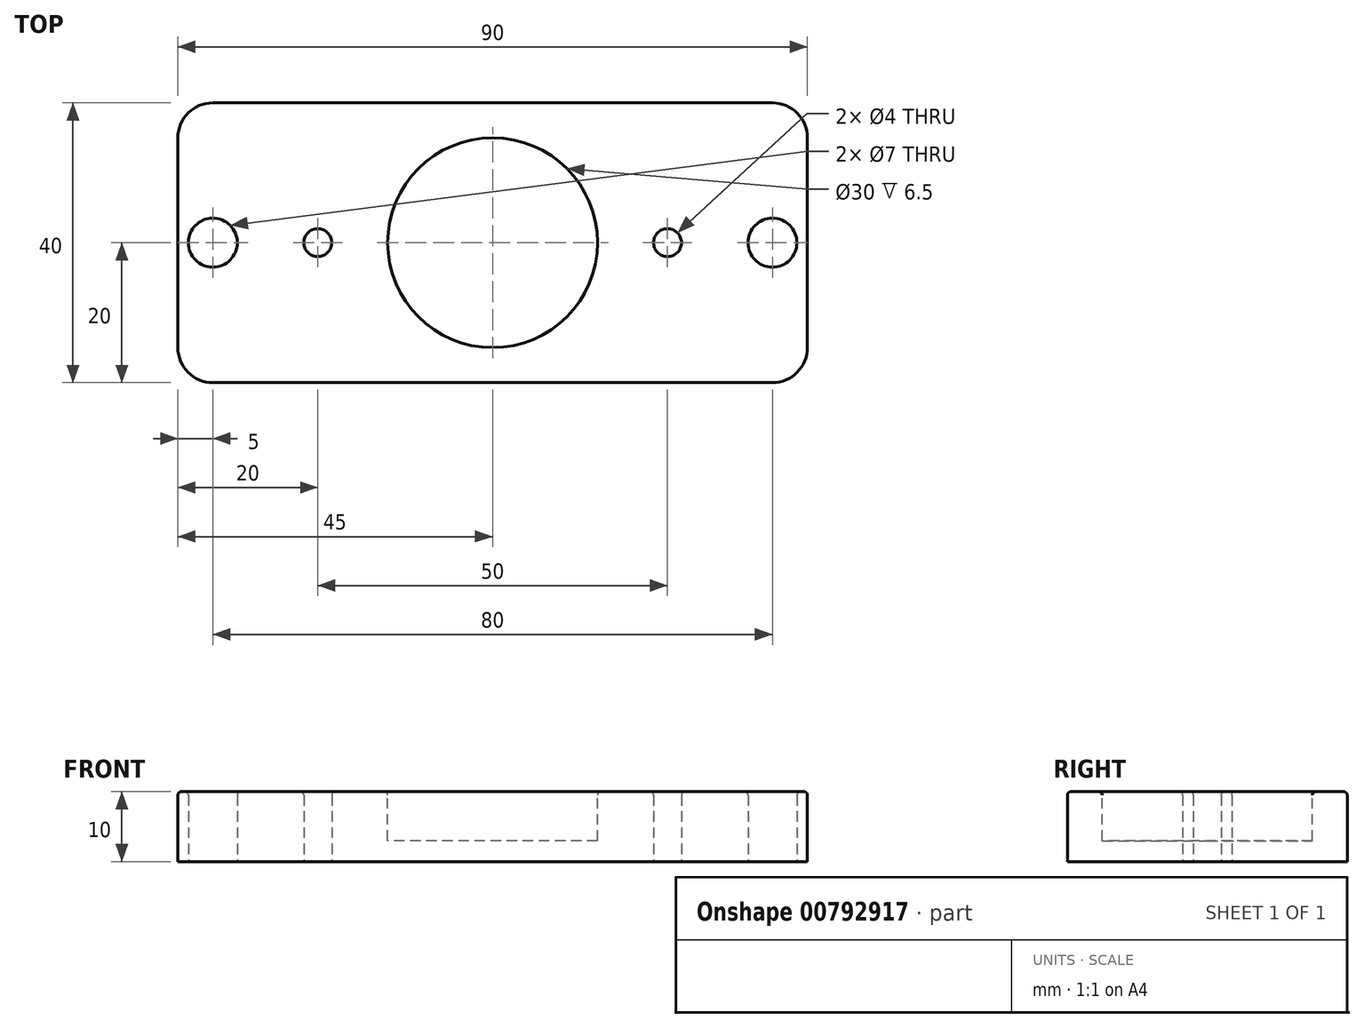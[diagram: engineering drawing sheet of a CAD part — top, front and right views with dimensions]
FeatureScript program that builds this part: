
annotation { "Feature Type Name" : "Feature", "Feature Type Description" : "" }
export const myFeature = defineFeature(function(context is Context, id is Id, definition is map)
    precondition{}
    {
        {
            var Q0;
            Q0=qCreatedBy(makeId("Top.planeOp"),FACE);
            var sketch = newSketch(context, id + "F0", { "sketchPlane" : qUnion([Q0])});
            skLineSegment(sketch, "E0.bottom", {"start": v(45, -20) * mm, "end": v(-45, -20) * mm});
            skLineSegment(sketch, "E0.top", {"start": v(45, 20) * mm, "end": v(-45, 20) * mm});
            skLineSegment(sketch, "E0.left", {"start": v(45, -20) * mm, "end": v(45, 20) * mm});
            skLineSegment(sketch, "E0.right", {"start": v(-45, -20) * mm, "end": v(-45, 20) * mm});
            skPoint(sketch, "E0.middle", {"position": v(0, 0) * mm});
            skCircle(sketch, "E1", {"center": v(-25, 0) * mm, "radius": 2 * mm});
            skCircle(sketch, "E2.MirrorC", {"center": v(25, 0) * mm, "radius": 2 * mm});
            skCircle(sketch, "E3", {"center": v(40, 0) * mm, "radius": 3.5 * mm});
            skCircle(sketch, "E4.MirrorC", {"center": v(-40, 0) * mm, "radius": 3.5 * mm});
            skSolve(sketch);
        }
        {
            var Q0;
            Q0 = qSketchRegion(id + "FLLW0Ii5PjXzbfg_0", true);
            var Q1;
            Q1 = qSketchRegion(id + "F0", true);
            extrude(context, id + "F1", {"entities" : qUnion([Q0, Q1]), "depth" : 10 * mm, "offsetDistance" : 25 * mm});
        }
        {
            var Q0;
            Q0=makeQuery(id+"F1.opExtrude","CAP_FACE",FACE,{"disambiguationData":[OSD([sQuery(id+"F0.wireOp",EDGE,"E0.bottom"),sQuery(id+"F0.wireOp",EDGE,"E0.top"),sQuery(id+"F0.wireOp",EDGE,"E0.left"),sQuery(id+"F0.wireOp",EDGE,"E0.right"),sQuery(id+"F0.wireOp",EDGE,"E1"),sQuery(id+"F0.wireOp",EDGE,"E2.MirrorC")])],"isStart":false});
            var sketch = newSketch(context, id + "F2", { "sketchPlane" : qUnion([Q0])});
            skCircle(sketch, "E5", {"center": v(0, 0) * mm, "radius": 15 * mm});
            skSolve(sketch);
        }
        {
            var Q0;
            Q0 = qSketchRegion(id + "F2", true);
            extrude(context, id + "F3", {"entities" : qUnion([Q0]), "operationType" : NewBodyOperationType.REMOVE, "oppositeDirection" : true, "depth" : 7 * mm, "offsetDistance" : 25 * mm});
        }
        {
            var Q0;
            Q0=makeQuery(id+"F1.opExtrude","CAP_FACE",FACE,{"disambiguationData":[OSD([sQuery(id+"F0.wireOp",EDGE,"E0.bottom"),sQuery(id+"F0.wireOp",EDGE,"E0.top"),sQuery(id+"F0.wireOp",EDGE,"E0.left"),sQuery(id+"F0.wireOp",EDGE,"E0.right"),sQuery(id+"F0.wireOp",EDGE,"E1"),sQuery(id+"F0.wireOp",EDGE,"E2.MirrorC")])],"isStart":false});
            fillet(context, id + "F4", {"entities" : qUnion([Q0]), "radius" : .5 * mm, "tangentPropagation" : true, "allowEdgeOverflow" : false});
        }
        {
            var Q0;
            Q0=makeQuery(id+"F1.opExtrude","SWEPT_EDGE",EDGE,{"disambiguationData":[OSD([sQuery(id+"F0.wireOp",EDGE,"E0.bottom"),sQuery(id+"F0.wireOp",EDGE,"E0.left")])]});
            var Q1;
            Q1=makeQuery(id+"F1.opExtrude","SWEPT_EDGE",EDGE,{"disambiguationData":[OSD([sQuery(id+"F0.wireOp",EDGE,"E0.bottom"),sQuery(id+"F0.wireOp",EDGE,"E0.right")])]});
            var Q2;
            Q2=makeQuery(id+"F1.opExtrude","SWEPT_EDGE",EDGE,{"disambiguationData":[OSD([sQuery(id+"F0.wireOp",EDGE,"E0.top"),sQuery(id+"F0.wireOp",EDGE,"E0.left")])]});
            var Q3;
            Q3=makeQuery(id+"F1.opExtrude","SWEPT_EDGE",EDGE,{"disambiguationData":[OSD([sQuery(id+"F0.wireOp",EDGE,"E0.top"),sQuery(id+"F0.wireOp",EDGE,"E0.right")])]});
            fillet(context, id + "F5", {"entities" : qUnion([Q0, Q1, Q2, Q3]), "radius" : 5 * mm, "tangentPropagation" : true, "allowEdgeOverflow" : false});
        }
    });
